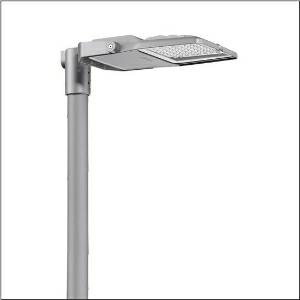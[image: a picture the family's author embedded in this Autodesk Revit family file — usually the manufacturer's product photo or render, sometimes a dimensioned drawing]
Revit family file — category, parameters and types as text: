
# Revit family: floodlight_fl_21_mini___pl43_5xa7775d2a3a_0001
name_source: partatom
category: Lighting Fixtures
units: mm (PartAtom-declared; Revit-internal decimal feet)

## family parameters
Cut with Voids When Loaded = No
Host = Face
Light Source = No
Part Type = Normal
Room Calculation Point = No
Round Connector Dimension = Use Diameter
Shared = No

## types (1)
- --- (1 x LED, 18300 lm, 142.9 W, 3000K)
    Apparent Load = 143 VA
    CIE Flux Codes = 27 78 99 100 100
    Color Rendering = 70
    Color Temperature = 3000K
    Default Elevation = 1800 mm
    Description = Floodlight FL 21 mini, floodlight, primary light control with lens, of PMMA, primary optical cover: protective disc, of toughened safety glass, transparent, light distribution: PL43, light emission: direct distribution, installation type: surface-mounted, LED, High Power LED, rated luminous flux: 18.300lm, luminous efficacy: 128lm/W, light colour: 730, colour temperature: 3000K, control gear: Smart Interface (Zhaga), control: flexible luminous flux parameterisation, time-dependent luminous flux control, constant luminous flux control, overheat protection, pre-setting: logarithmic dimming characteristic, with terminal, 6-pole, mains connection: 220..240V, AC, 50/60Hz, start of lifetime: 143W, end of service life: 151W, reduction: 63W, luminaire housing, of diecast aluminium, powder-coated, Siteco® metallic grey (DB 702S), corrosivity category C5 mid according to DIN EN ISO 12944, suitable for swimming pools, chlorine-resistant, sealing non-destructively replaceable, please order mast flange separately, mast bracket, of steel, galvanised, powder-coated, Siteco® metallic grey (DB 702S), Smart Interface above, protection rating (complete): IP66, insulation class (complete): insulation class II (safety insulation), certification: CE, ENEC, VDE, protection symbol: D, impact resistance: IK08, permissible operating ambient temperature: -40..+40°C, permissible operating ambient temperature for outdoor applications: -40..+50°C, standard: DIN EN 12944, LABS conformity tested according to VDMA 24364:2018-05, packaging unit: 1 piece

Light Distribution: PL43
    Height = 70 mm
    Lamp = 1 x LED
    Lamp Light Flux = 18300 lm
    Lamp Power = 142.9 W
    Lamp count = 1
    Length = 485 mm
    Luminous efficacy = 128 lm/W
    Manufacturer = Siteco
    ModVariant = No
    Model = 5XA7775D2A3A
    Number of Poles = 1
    OnlyDefault = Yes
    Power Factor = 1
    Product Name = Floodlight FL 21 mini | PL43
    Product group = floodlight | pylon annexe
    ProductGroupID = 6201
    Protection Class = Protection class II
    Protection Degree = IP 66
    RLX_Detail_Level = 1
    RLX_Emergency_Light_Flux = 0 lm
    RLX_Emergency_Type = 0
    RLX_Emergency_Type_DB = No
    RlxData = <blob elided: 101301 chars, md5=7f072446>
    Socket = socket
    Standby Power = 0 W
    System Light Flux = 18300 lm
    System Power = 143 W
    Type Comments = factory setting: luminous flux: 100 % | dim-lin: 254 | 730 mA
    Type Image = l_1007125.jpg
    URL = http://relux.com
    VarID = @adj_182429
    Voltage = 0 V
    Weight = 0.00 kg
    Width = 337 mm

## geometry (parser evidence)
native form markers: Blend x4, Sweep x13
no freeform markers — native parametric forms only
